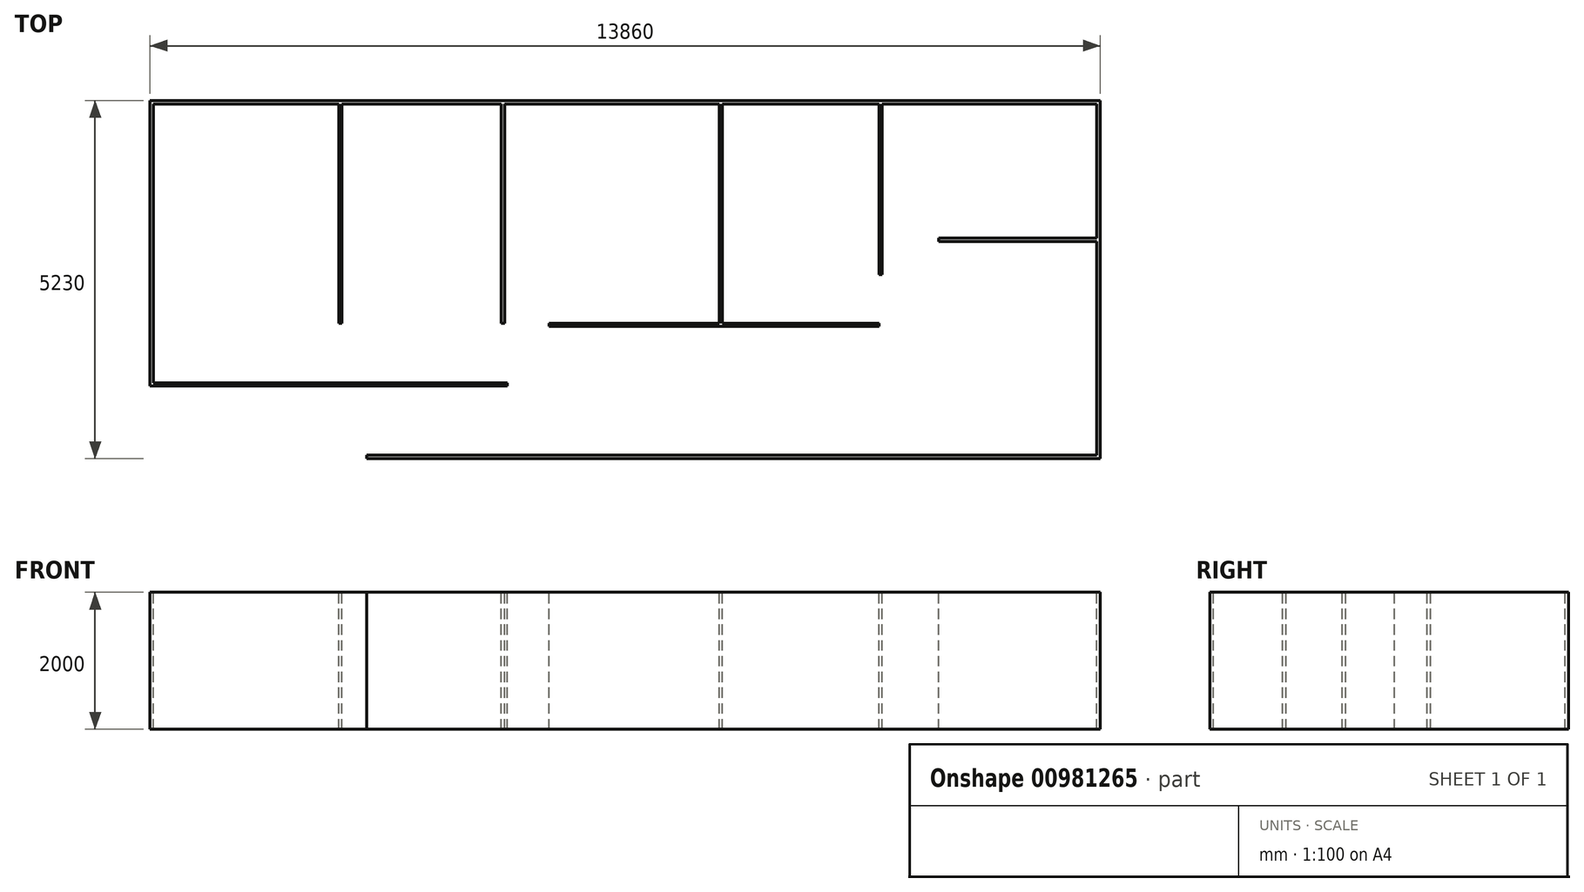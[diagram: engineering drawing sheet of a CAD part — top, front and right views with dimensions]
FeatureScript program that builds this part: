
annotation { "Feature Type Name" : "Feature", "Feature Type Description" : "" }
export const myFeature = defineFeature(function(context is Context, id is Id, definition is map)
    precondition{}
    {
        {
            var Q0;
            Q0=qCreatedBy(makeId("Top.planeOp"),FACE);
            var sketch = newSketch(context, id + "F0", { "sketchPlane" : qUnion([Q0])});
            skLineSegment(sketch, "E0", {"start": v(0, 0) * mm, "end": v(10650, 0) * mm});
            skLineSegment(sketch, "E1", {"start": v(10650, 0) * mm, "end": v(10650, 3120) * mm});
            skLineSegment(sketch, "E2", {"start": v(10650, 5130) * mm, "end": v(7520, 5130) * mm});
            skLineSegment(sketch, "E3", {"start": v(-3110, 5130) * mm, "end": v(-3110, 1060) * mm});
            skLineSegment(sketch, "E4", {"start": v(-3110, 1060) * mm, "end": v(0, 1060) * mm});
            skLineSegment(sketch, "E5", {"start": v(0, 1060) * mm, "end": v(2050, 1060) * mm});
            skLineSegment(sketch, "E6", {"start": v(10650, 3170) * mm, "end": v(8340, 3170) * mm});
            skLineSegment(sketch, "E7", {"start": v(7470, 5130) * mm, "end": v(7470, 2640) * mm});
            skLineSegment(sketch, "E8", {"start": v(5190, 5130) * mm, "end": v(5190, 1930) * mm});
            skLineSegment(sketch, "E9", {"start": v(1960, 5130) * mm, "end": v(1960, 1930) * mm});
            skLineSegment(sketch, "E10", {"start": v(-410, 1930) * mm, "end": v(-410, 5130) * mm});
            skPoint(sketch, "E11", {"position": v(2660, 1930) * mm});
            skLineSegment(sketch, "E12", {"start": v(2660, 1930) * mm, "end": v(5140, 1930) * mm});
            skLineSegment(sketch, "E13.2", {"start": v(0, -50) * mm, "end": v(10700, -50) * mm});
            skLineSegment(sketch, "E13.3", {"start": v(10700, -50) * mm, "end": v(10700, 5180) * mm});
            skLineSegment(sketch, "E13.4", {"start": v(10700, 5180) * mm, "end": v(-3160, 5180) * mm});
            skLineSegment(sketch, "E13.5", {"start": v(-3160, 5180) * mm, "end": v(-3160, 1010) * mm});
            skLineSegment(sketch, "E14", {"start": v(-3160, 1010) * mm, "end": v(2050, 1010) * mm});
            skLineSegment(sketch, "E15", {"start": v(2050, 1010) * mm, "end": v(2050, 1060) * mm});
            skLineSegment(sketch, "E16.0", {"start": v(-360, 1930) * mm, "end": v(-360, 5130) * mm});
            skLineSegment(sketch, "E17.0", {"start": v(2010, 5130) * mm, "end": v(2010, 1930) * mm});
            skLineSegment(sketch, "E18.0", {"start": v(5140, 5130) * mm, "end": v(5140, 1930) * mm});
            skLineSegment(sketch, "E19.0", {"start": v(2660, 1880) * mm, "end": v(7470, 1880) * mm});
            skLineSegment(sketch, "E20.0", {"start": v(7520, 5130) * mm, "end": v(7520, 2640) * mm});
            skLineSegment(sketch, "E21", {"start": v(-410, 1930) * mm, "end": v(-360, 1930) * mm});
            skLineSegment(sketch, "E22", {"start": v(1960, 1930) * mm, "end": v(2010, 1930) * mm});
            skLineSegment(sketch, "E23", {"start": v(2660, 1880) * mm, "end": v(2660, 1930) * mm});
            skLineSegment(sketch, "E24", {"start": v(7520, 2640) * mm, "end": v(7470, 2640) * mm});
            skLineSegment(sketch, "E25", {"start": v(7470, 1930) * mm, "end": v(7470, 1880) * mm});
            skLineSegment(sketch, "E26.0", {"start": v(10650, 3120) * mm, "end": v(8340, 3120) * mm});
            skLineSegment(sketch, "E27", {"start": v(8340, 3170) * mm, "end": v(8340, 3120) * mm});
            skLineSegment(sketch, "E28.trimOffspring", {"start": v(5140, 5130) * mm, "end": v(2010, 5130) * mm});
            skLineSegment(sketch, "E29.trimOffspring", {"start": v(1960, 5130) * mm, "end": v(-360, 5130) * mm});
            skLineSegment(sketch, "E30.trimOffspring", {"start": v(-410, 5130) * mm, "end": v(-3110, 5130) * mm});
            skLineSegment(sketch, "E31.trimOffspring", {"start": v(10650, 3170) * mm, "end": v(10650, 5130) * mm});
            skLineSegment(sketch, "E32.trimOffspring", {"start": v(5190, 1930) * mm, "end": v(7470, 1930) * mm});
            skLineSegment(sketch, "E33.trimOffspring", {"start": v(7470, 5130) * mm, "end": v(5190, 5130) * mm});
            skLineSegment(sketch, "E34", {"start": v(0, -50) * mm, "end": v(0, 0) * mm});
            skSolve(sketch);
        }
        {
            var Q0;
            Q0 = qSketchRegion(id + "F0", true);
            extrude(context, id + "F1", {"entities" : qUnion([Q0]), "oppositeDirection" : true, "depth" : 2000 * mm, "offsetDistance" : 25.4 * mm});
        }
    });
